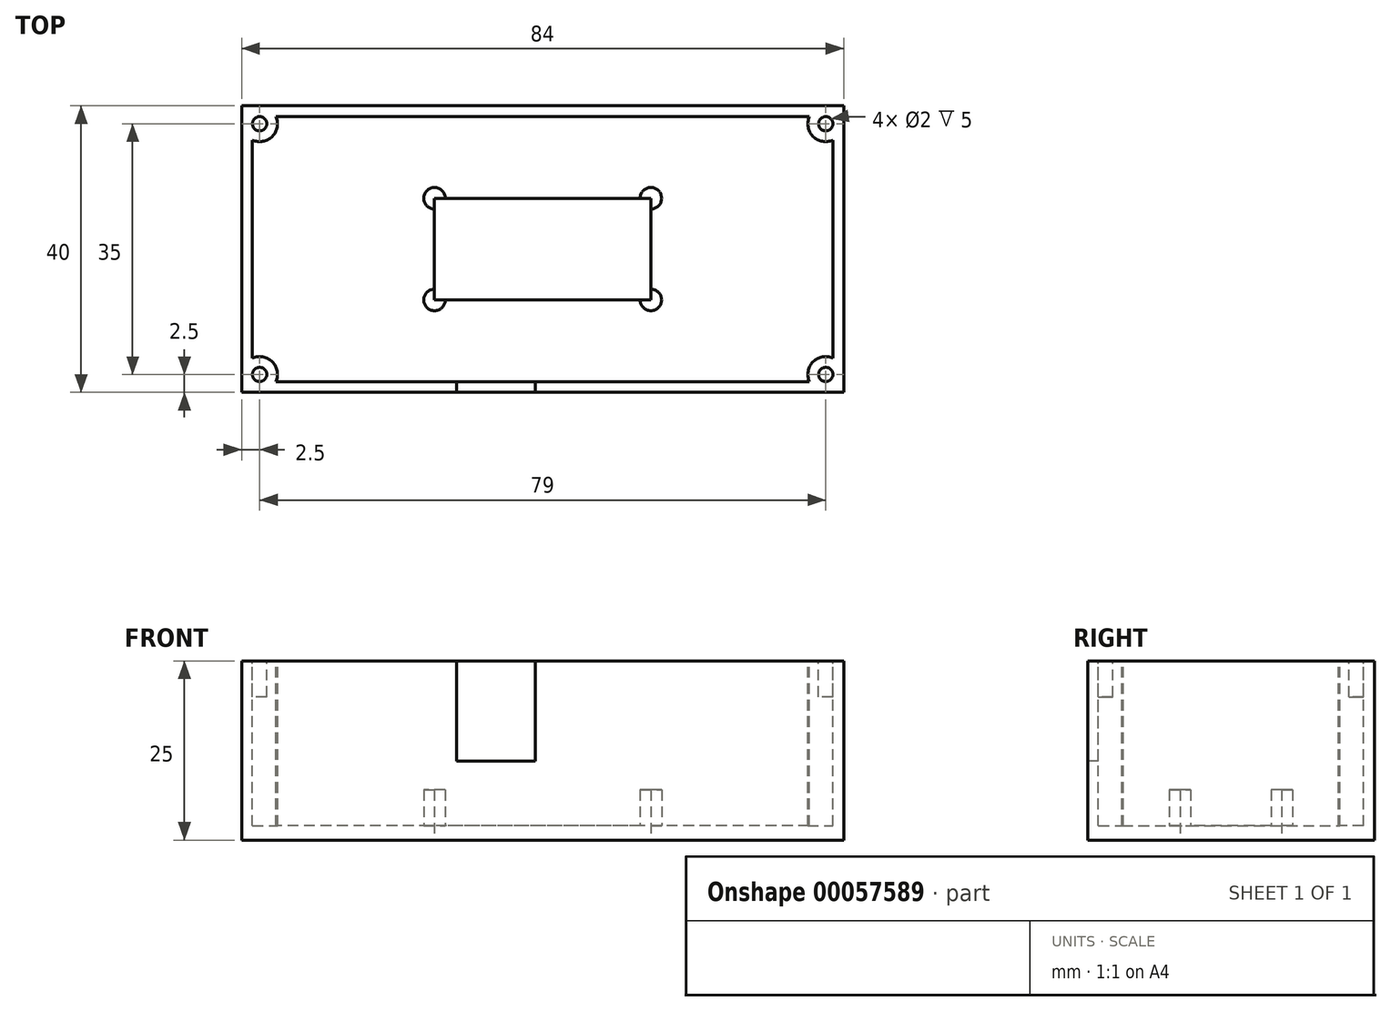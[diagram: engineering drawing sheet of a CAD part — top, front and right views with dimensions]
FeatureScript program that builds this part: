
annotation { "Feature Type Name" : "Feature", "Feature Type Description" : "" }
export const myFeature = defineFeature(function(context is Context, id is Id, definition is map)
    precondition{}
    {
        {
            var Q0;
            Q0=qCreatedBy(makeId("Top.planeOp"),FACE);
            var sketch = newSketch(context, id + "F0", { "sketchPlane" : qUnion([Q0])});
            skLineSegment(sketch, "E0.rect.bottom", {"start": v(42, -20) * mm, "end": v(-42, -20) * mm});
            skLineSegment(sketch, "E0.rect.top", {"start": v(42, 20) * mm, "end": v(-42, 20) * mm});
            skLineSegment(sketch, "E0.rect.left", {"start": v(42, -20) * mm, "end": v(42, 20) * mm});
            skLineSegment(sketch, "E0.rect.right", {"start": v(-42, -20) * mm, "end": v(-42, 20) * mm});
            skPoint(sketch, "E0.rect.middle", {"position": v(0, 0) * mm});
            skLineSegment(sketch, "E1.rect.bottom", {"start": v(15.1, 7.1) * mm, "end": v(-15.1, 7.1) * mm});
            skLineSegment(sketch, "E1.rect.top", {"start": v(15.1, -7.1) * mm, "end": v(-15.1, -7.1) * mm});
            skLineSegment(sketch, "E1.rect.left", {"start": v(15.1, 7.1) * mm, "end": v(15.1, -7.1) * mm});
            skLineSegment(sketch, "E1.rect.right", {"start": v(-15.1, 7.1) * mm, "end": v(-15.1, -7.1) * mm});
            skSolve(sketch);
        }
        {
            var Q0;
            Q0=makeQuery(id+"F0.imprint","IMPRINT",FACE,{"disambiguationData":[TD([[makeQuery(id+"F0.imprint","IMPRINT",EDGE,{"derivedFrom":sQuery(id+"F0.wireOp",EDGE,"E0.rect.bottom")}),-1.0]])]});
            extrude(context, id + "F1", {"entities" : qUnion([Q0]), "depth" : 25 * mm});
        }
        {
            var Q0;
            Q0=makeQuery(id+"F1.opExtrude","CAP_FACE",FACE,{"disambiguationData":[OSD([sQuery(id+"F0.wireOp",EDGE,"E0.rect.bottom"),sQuery(id+"F0.wireOp",EDGE,"E0.rect.top"),sQuery(id+"F0.wireOp",EDGE,"E0.rect.left"),sQuery(id+"F0.wireOp",EDGE,"E0.rect.right")])],"isStart":false});
            var sketch = newSketch(context, id + "F2", { "sketchPlane" : qUnion([Q0])});
            skLineSegment(sketch, "E2.rect.bottom", {"start": v(40.5, -18.5) * mm, "end": v(-40.5, -18.5) * mm});
            skLineSegment(sketch, "E2.rect.top", {"start": v(40.5, 18.5) * mm, "end": v(-40.5, 18.5) * mm});
            skLineSegment(sketch, "E2.rect.left", {"start": v(40.5, -18.5) * mm, "end": v(40.5, 18.5) * mm});
            skLineSegment(sketch, "E2.rect.right", {"start": v(-40.5, -18.5) * mm, "end": v(-40.5, 18.5) * mm});
            skPoint(sketch, "E2.rect.middle", {"position": v(0, 0) * mm});
            skCircle(sketch, "E3", {"center": v(-39.5, 17.5) * mm, "radius": 2.5 * mm});
            skCircle(sketch, "E4", {"center": v(39.5, 17.5) * mm, "radius": 2.5 * mm});
            skCircle(sketch, "E5", {"center": v(39.5, -17.5) * mm, "radius": 2.5 * mm});
            skCircle(sketch, "E6", {"center": v(-39.5, -17.5) * mm, "radius": 2.5 * mm});
            skSolve(sketch);
        }
        {
            var Q0;
            Q0=makeQuery(id+"F2.imprint","IMPRINT",FACE,{"disambiguationData":[TD([[makeQuery(id+"F2.imprint","IMPRINT",EDGE,{"derivedFrom":makeQuery(id+"F1.opExtrude","CAP_EDGE",EDGE,{"disambiguationData":[OSD([sQuery(id+"F0.wireOp",EDGE,"E1.rect.bottom")])],"isStart":false})}),-1.0]])]});
            extrude(context, id + "F3", {"entities" : qUnion([Q0]), "operationType" : NewBodyOperationType.REMOVE, "oppositeDirection" : true, "depth" : 23 * mm});
        }
        {
            var Q0;
            Q0=makeQuery(id+"F3.boolean.opBoolean","COPY",FACE,{"derivedFrom":makeQuery(id+"F3.opExtrude","CAP_FACE",FACE,{"disambiguationData":[OSD([sQuery(id+"F0.wireOp",EDGE,"E1.rect.bottom"),sQuery(id+"F0.wireOp",EDGE,"E1.rect.top"),sQuery(id+"F0.wireOp",EDGE,"E1.rect.left"),sQuery(id+"F0.wireOp",EDGE,"E1.rect.right"),sQuery(id+"F2.wireOp",EDGE,"E2.rect.bottom"),sQuery(id+"F2.wireOp",EDGE,"E2.rect.top"),sQuery(id+"F2.wireOp",EDGE,"E2.rect.left"),sQuery(id+"F2.wireOp",EDGE,"E2.rect.right"),sQuery(id+"F2.wireOp",EDGE,"E3"),sQuery(id+"F2.wireOp",EDGE,"E4"),sQuery(id+"F2.wireOp",EDGE,"E5"),sQuery(id+"F2.wireOp",EDGE,"E6")])],"isStart":false})});
            var sketch = newSketch(context, id + "F4", { "sketchPlane" : qUnion([Q0])});
            skArc(sketch, "E7", {"start": v(-13.6, 7.1) * mm, "mid": v(-16.16, 8.16) * mm, "end": v(-15.1, 5.6) * mm});
            skArc(sketch, "E8", {"start": v(13.6, -7.1) * mm, "mid": v(16.16, -8.16) * mm, "end": v(15.1, -5.6) * mm});
            skArc(sketch, "E9", {"start": v(-15.1, -5.6) * mm, "mid": v(-16.16, -8.16) * mm, "end": v(-13.6, -7.1) * mm});
            skArc(sketch, "E10", {"start": v(15.1, 5.6) * mm, "mid": v(16.16, 8.16) * mm, "end": v(13.6, 7.1) * mm});
            skLineSegment(sketch, "E11.rect.bottom", {"start": v(15.1, 7.1) * mm, "end": v(13.6, 7.1) * mm});
            skLineSegment(sketch, "E11.rect.top", {"start": v(15.1, -7.1) * mm, "end": v(13.6, -7.1) * mm});
            skLineSegment(sketch, "E11.rect.left", {"start": v(15.1, 7.1) * mm, "end": v(15.1, 5.6) * mm});
            skLineSegment(sketch, "E11.rect.right", {"start": v(-15.1, 7.1) * mm, "end": v(-15.1, 5.6) * mm});
            skPoint(sketch, "E11.rect.middle", {"position": v(0, 0) * mm});
            skLineSegment(sketch, "E12.trimOffspring", {"start": v(-15.1, -5.6) * mm, "end": v(-15.1, -7.1) * mm});
            skLineSegment(sketch, "E13.trimOffspring", {"start": v(-13.6, 7.1) * mm, "end": v(-15.1, 7.1) * mm});
            skLineSegment(sketch, "E14.trimOffspring", {"start": v(15.1, -5.6) * mm, "end": v(15.1, -7.1) * mm});
            skLineSegment(sketch, "E15.trimOffspring", {"start": v(-13.6, -7.1) * mm, "end": v(-15.1, -7.1) * mm});
            skSolve(sketch);
        }
        {
            var Q0;
            Q0=makeQuery(id+"F4.imprint","IMPRINT",FACE,{"disambiguationData":[TD([[makeQuery(id+"F4.imprint","IMPRINT",EDGE,{"derivedFrom":sQuery(id+"F4.wireOp",EDGE,"E7")}),1.0]])]});
            var Q1;
            Q1=makeQuery(id+"F4.imprint","IMPRINT",FACE,{"disambiguationData":[TD([[makeQuery(id+"F4.imprint","IMPRINT",EDGE,{"derivedFrom":sQuery(id+"F4.wireOp",EDGE,"E9")}),1.0]])]});
            var Q2;
            Q2=makeQuery(id+"F4.imprint","IMPRINT",FACE,{"disambiguationData":[TD([[makeQuery(id+"F4.imprint","IMPRINT",EDGE,{"derivedFrom":sQuery(id+"F4.wireOp",EDGE,"E8")}),1.0]])]});
            var Q3;
            Q3=makeQuery(id+"F4.imprint","IMPRINT",FACE,{"disambiguationData":[TD([[makeQuery(id+"F4.imprint","IMPRINT",EDGE,{"derivedFrom":sQuery(id+"F4.wireOp",EDGE,"E10")}),1.0]])]});
            extrude(context, id + "F5", {"entities" : qUnion([Q0, Q1, Q2, Q3]), "operationType" : NewBodyOperationType.ADD, "depth" : 5 * mm});
        }
        {
            var Q0;
            Q0=makeQuery(id+"F1.opExtrude","CAP_FACE",FACE,{"disambiguationData":[OSD([sQuery(id+"F0.wireOp",EDGE,"E0.rect.bottom"),sQuery(id+"F0.wireOp",EDGE,"E0.rect.top"),sQuery(id+"F0.wireOp",EDGE,"E0.rect.left"),sQuery(id+"F0.wireOp",EDGE,"E0.rect.right"),sQuery(id+"F0.wireOp",EDGE,"E1.rect.bottom"),sQuery(id+"F0.wireOp",EDGE,"E1.rect.top"),sQuery(id+"F0.wireOp",EDGE,"E1.rect.left"),sQuery(id+"F0.wireOp",EDGE,"E1.rect.right")])],"isStart":false});
            var sketch = newSketch(context, id + "F6", { "sketchPlane" : qUnion([Q0])});
            skCircle(sketch, "E16", {"center": v(-39.5, 17.5) * mm, "radius": 1 * mm});
            skCircle(sketch, "E17", {"center": v(39.5, 17.5) * mm, "radius": 1 * mm});
            skCircle(sketch, "E18", {"center": v(39.5, -17.5) * mm, "radius": 1 * mm});
            skCircle(sketch, "E19", {"center": v(-39.5, -17.5) * mm, "radius": 1 * mm});
            skSolve(sketch);
        }
        {
            var Q0;
            Q0 = qSketchRegion(id + "F6", true);
            extrude(context, id + "F7", {"entities" : qUnion([Q0]), "operationType" : NewBodyOperationType.REMOVE, "oppositeDirection" : true, "depth" : 5 * mm});
        }
        {
            var Q0;
            Q0=makeQuery(id+"F1.opExtrude","SWEPT_FACE",FACE,{"disambiguationData":[OSD([sQuery(id+"F0.wireOp",EDGE,"E0.rect.bottom")])]});
            var sketch = newSketch(context, id + "F8", { "sketchPlane" : qUnion([Q0])});
            skLineSegment(sketch, "E20.bottom", {"start": v(-12, 11) * mm, "end": v(-1, 11) * mm});
            skLineSegment(sketch, "E20.top", {"start": v(-12, 20) * mm, "end": v(-1, 20) * mm});
            skLineSegment(sketch, "E20.left", {"start": v(-12, 11) * mm, "end": v(-12, 20) * mm});
            skLineSegment(sketch, "E20.right", {"start": v(-1, 11) * mm, "end": v(-1, 20) * mm});
            skLineSegment(sketch, "E21", {"start": v(-12, 20) * mm, "end": v(-12, 25) * mm});
            skLineSegment(sketch, "E22", {"start": v(-1, 20) * mm, "end": v(-1, 25) * mm});
            skSolve(sketch);
        }
        {
            var Q0;
            Q0=makeQuery(id+"F8.imprint","IMPRINT",FACE,{"disambiguationData":[TD([[makeQuery(id+"F8.imprint","IMPRINT",EDGE,{"derivedFrom":sQuery(id+"F8.wireOp",EDGE,"E20.bottom")}),1.0]])]});
            var Q1;
            Q1=makeQuery(id+"F8.imprint","IMPRINT",FACE,{"disambiguationData":[TD([[makeQuery(id+"F8.imprint","IMPRINT",EDGE,{"derivedFrom":sQuery(id+"F8.wireOp",EDGE,"E20.top")}),1.0]])]});
            extrude(context, id + "F9", {"entities" : qUnion([Q0, Q1]), "operationType" : NewBodyOperationType.REMOVE, "endBound" : BoundingType.UP_TO_NEXT, "oppositeDirection" : true, "depth" : 25 * mm});
        }
    });
